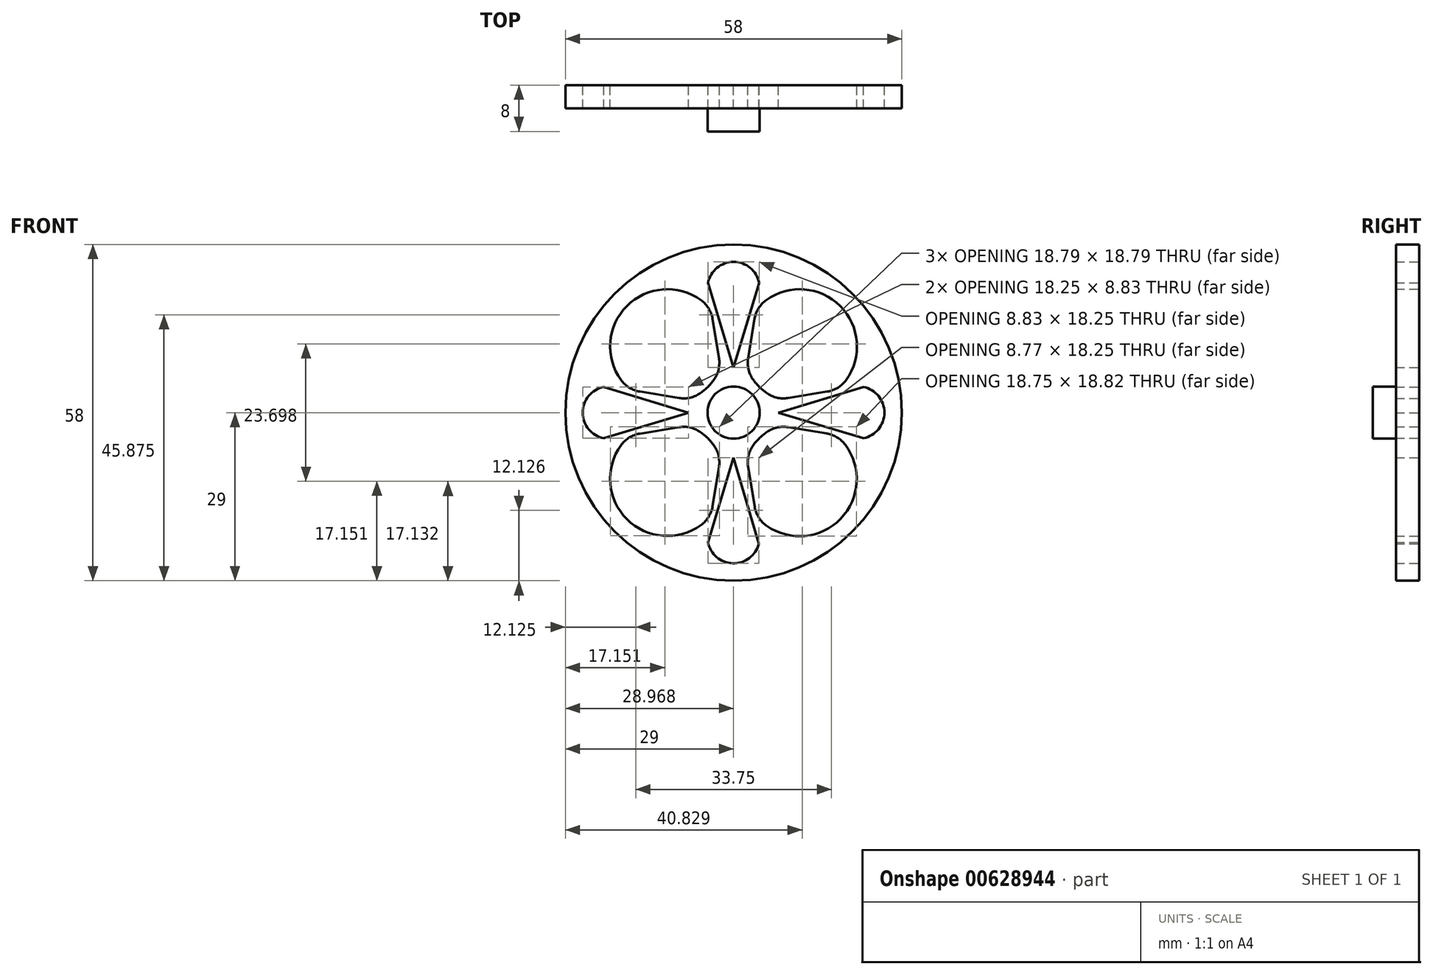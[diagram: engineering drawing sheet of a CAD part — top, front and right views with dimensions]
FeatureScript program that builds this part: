
annotation { "Feature Type Name" : "Feature", "Feature Type Description" : "" }
export const myFeature = defineFeature(function(context is Context, id is Id, definition is map)
    precondition{}
    {
        {
            var Q0;
            Q0=qCreatedBy(makeId("Front.planeOp"),FACE);
            var sketch = newSketch(context, id + "F0", { "sketchPlane" : qUnion([Q0])});
            skCircle(sketch, "E0", {"center": v(0, 0) * mm, "radius": 27 * mm});
            skCircle(sketch, "E1", {"center": v(0, 0) * mm, "radius": 4.5 * mm});
            skCircle(sketch, "E2", {"center": v(0, 0) * mm, "radius": 29 * mm});
            skArc(sketch, "E3", {"start": v(-22.37, 4.42) * mm, "mid": v(-26, 0) * mm, "end": v(-22.37, -4.42) * mm});
            skArc(sketch, "E4", {"start": v(4.42, 22.37) * mm, "mid": v(0, 26) * mm, "end": v(-4.42, 22.37) * mm});
            skArc(sketch, "E5", {"start": v(22.37, -4.42) * mm, "mid": v(26, 0) * mm, "end": v(22.37, 4.42) * mm});
            skArc(sketch, "E6", {"start": v(-4.42, -22.37) * mm, "mid": v(-0.14, -26) * mm, "end": v(4.35, -22.65) * mm});
            skPoint(sketch, "E7.orphan", {"position": v(-55.65, 0) * mm});
            skLineSegment(sketch, "E8", {"start": v(-16.16, 3.63) * mm, "end": v(-9.39, 2.52) * mm});
            skLineSegment(sketch, "E9", {"start": v(-16.16, -3.63) * mm, "end": v(-9.39, -2.52) * mm});
            skLineSegment(sketch, "E10", {"start": v(-2.52, -9.39) * mm, "end": v(-3.63, -16.16) * mm});
            skLineSegment(sketch, "E11", {"start": v(2.52, -9.37) * mm, "end": v(3.64, -16.26) * mm});
            skLineSegment(sketch, "E12", {"start": v(9.4, -2.52) * mm, "end": v(16.06, -3.6) * mm});
            skLineSegment(sketch, "E13", {"start": v(9.39, 2.52) * mm, "end": v(16.16, 3.63) * mm});
            skLineSegment(sketch, "E14", {"start": v(2.52, 9.39) * mm, "end": v(3.63, 16.16) * mm});
            skArc(sketch, "E15", {"start": v(5.76, -3.34) * mm, "mid": v(4.5, -4.37) * mm, "end": v(3.43, -5.6) * mm});
            skPoint(sketch, "E15.third.point", {"position": v(18.33, -18.44) * mm});
            skArc(sketch, "E16", {"start": v(19.4, 5.63) * mm, "mid": v(18.38, 18.38) * mm, "end": v(5.63, 19.4) * mm});
            skPoint(sketch, "E16.third.point", {"position": v(16.77, 19.7) * mm});
            skArc(sketch, "E17", {"start": v(-19.4, -5.63) * mm, "mid": v(-18.38, -18.38) * mm, "end": v(-5.63, -19.4) * mm});
            skPoint(sketch, "E17.third.point", {"position": v(-19.92, -16.4) * mm});
            skArc(sketch, "E18", {"start": v(-5.67, 3.38) * mm, "mid": v(-4.43, 4.43) * mm, "end": v(-3.38, 5.67) * mm});
            skPoint(sketch, "E18.third.point", {"position": v(-19.3, 17.32) * mm});
            skLineSegment(sketch, "E19", {"start": v(0, 7.75) * mm, "end": v(-4.42, 22.37) * mm});
            skLineSegment(sketch, "E20", {"start": v(4.42, 22.37) * mm, "end": v(0, 7.75) * mm});
            skLineSegment(sketch, "E21", {"start": v(7.75, 0) * mm, "end": v(14.26, 1.97) * mm});
            skLineSegment(sketch, "E22", {"start": v(22.37, -4.42) * mm, "end": v(7.75, 0) * mm});
            skLineSegment(sketch, "E23", {"start": v(-7.75, 0) * mm, "end": v(-22.37, 4.42) * mm});
            skLineSegment(sketch, "E24", {"start": v(-22.37, -4.42) * mm, "end": v(-7.75, 0) * mm});
            skLineSegment(sketch, "E25", {"start": v(0, -7.75) * mm, "end": v(-4.42, -22.37) * mm});
            skLineSegment(sketch, "E26", {"start": v(4.35, -22.65) * mm, "end": v(0, -7.75) * mm});
            skArc(sketch, "E27.trimOffspring", {"start": v(-3.38, -5.67) * mm, "mid": v(-4.43, -4.43) * mm, "end": v(-5.67, -3.38) * mm});
            skArc(sketch, "E28.trimOffspring", {"start": v(5.71, -19.55) * mm, "mid": v(18.45, -18.32) * mm, "end": v(19.26, -5.55) * mm});
            skLineSegment(sketch, "E29", {"start": v(14.26, 1.97) * mm, "end": v(22.37, 4.42) * mm});
            skArc(sketch, "E30.trimOffspring", {"start": v(3.38, 5.67) * mm, "mid": v(4.43, 4.43) * mm, "end": v(5.67, 3.38) * mm});
            skArc(sketch, "E31.trimOffspring", {"start": v(-5.63, 19.4) * mm, "mid": v(-18.38, 18.38) * mm, "end": v(-19.4, 5.63) * mm});
            skLineSegment(sketch, "E32.trimOffspring", {"start": v(-3.63, 16.16) * mm, "end": v(-2.52, 9.39) * mm});
            skPoint(sketch, "E33.visualSharp", {"position": v(-7.75, 2.25) * mm});
            skArc(sketch, "E33.filletArc", {"start": v(-9.39, 2.52) * mm, "mid": v(-7.45, 2.58) * mm, "end": v(-5.67, 3.38) * mm});
            skPoint(sketch, "E34.visualSharp", {"position": v(-17.8, 3.9) * mm});
            skArc(sketch, "E34.filletArc", {"start": v(-19.4, 5.63) * mm, "mid": v(-17.98, 4.3) * mm, "end": v(-16.16, 3.63) * mm});
            skPoint(sketch, "E35.visualSharp", {"position": v(-3.9, 17.8) * mm});
            skArc(sketch, "E35.filletArc", {"start": v(-3.63, 16.16) * mm, "mid": v(-4.3, 17.98) * mm, "end": v(-5.63, 19.4) * mm});
            skPoint(sketch, "E36.visualSharp", {"position": v(-2.25, 7.75) * mm});
            skArc(sketch, "E36.filletArc", {"start": v(-3.38, 5.67) * mm, "mid": v(-2.58, 7.45) * mm, "end": v(-2.52, 9.39) * mm});
            skPoint(sketch, "E37.visualSharp", {"position": v(7.8, -2.26) * mm});
            skArc(sketch, "E37.filletArc", {"start": v(9.4, -2.52) * mm, "mid": v(7.5, -2.58) * mm, "end": v(5.76, -3.34) * mm});
            skPoint(sketch, "E38.visualSharp", {"position": v(2.24, -7.7) * mm});
            skArc(sketch, "E38.filletArc", {"start": v(3.43, -5.6) * mm, "mid": v(2.6, -7.4) * mm, "end": v(2.52, -9.37) * mm});
            skPoint(sketch, "E39.visualSharp", {"position": v(17.66, -3.87) * mm});
            skArc(sketch, "E39.filletArc", {"start": v(19.26, -5.55) * mm, "mid": v(17.85, -4.27) * mm, "end": v(16.06, -3.6) * mm});
            skPoint(sketch, "E40.visualSharp", {"position": v(-2.25, -7.75) * mm});
            skArc(sketch, "E40.filletArc", {"start": v(-2.52, -9.39) * mm, "mid": v(-2.58, -7.45) * mm, "end": v(-3.38, -5.67) * mm});
            skPoint(sketch, "E41.visualSharp", {"position": v(-7.75, -2.25) * mm});
            skArc(sketch, "E41.filletArc", {"start": v(-5.67, -3.38) * mm, "mid": v(-7.45, -2.58) * mm, "end": v(-9.39, -2.52) * mm});
            skPoint(sketch, "E42.visualSharp", {"position": v(3.92, -17.93) * mm});
            skArc(sketch, "E42.filletArc", {"start": v(3.64, -16.26) * mm, "mid": v(4.34, -18.11) * mm, "end": v(5.71, -19.55) * mm});
            skPoint(sketch, "E43.visualSharp", {"position": v(-3.9, -17.8) * mm});
            skArc(sketch, "E43.filletArc", {"start": v(-5.63, -19.4) * mm, "mid": v(-4.3, -17.98) * mm, "end": v(-3.63, -16.16) * mm});
            skPoint(sketch, "E44.visualSharp", {"position": v(-17.8, -3.9) * mm});
            skArc(sketch, "E44.filletArc", {"start": v(-16.16, -3.63) * mm, "mid": v(-17.98, -4.3) * mm, "end": v(-19.4, -5.63) * mm});
            skPoint(sketch, "E45.visualSharp", {"position": v(17.8, 3.9) * mm});
            skArc(sketch, "E45.filletArc", {"start": v(16.16, 3.63) * mm, "mid": v(17.98, 4.3) * mm, "end": v(19.4, 5.63) * mm});
            skPoint(sketch, "E46.visualSharp", {"position": v(7.75, 2.25) * mm});
            skArc(sketch, "E46.filletArc", {"start": v(5.67, 3.38) * mm, "mid": v(7.45, 2.58) * mm, "end": v(9.39, 2.52) * mm});
            skPoint(sketch, "E47.visualSharp", {"position": v(2.25, 7.75) * mm});
            skArc(sketch, "E47.filletArc", {"start": v(2.52, 9.39) * mm, "mid": v(2.58, 7.45) * mm, "end": v(3.38, 5.67) * mm});
            skPoint(sketch, "E48.visualSharp", {"position": v(3.9, 17.8) * mm});
            skArc(sketch, "E48.filletArc", {"start": v(5.63, 19.4) * mm, "mid": v(4.3, 17.98) * mm, "end": v(3.63, 16.16) * mm});
            skSolve(sketch);
        }
        {
            var Q0;
            Q0=makeQuery(id+"F0.imprint","IMPRINT",FACE,{"disambiguationData":[TD([[makeQuery(id+"F0.imprint","IMPRINT",EDGE,{"derivedFrom":sQuery(id+"F0.wireOp",EDGE,"E1")}),1.0]])]});
            extrude(context, id + "F1", {"entities" : qUnion([Q0]), "depth" : 8 * mm, "offsetDistance" : 25 * mm});
        }
        {
            var Q0;
            Q0=makeQuery(id+"F0.imprint","IMPRINT",FACE,{"disambiguationData":[TD([[makeQuery(id+"F0.imprint","IMPRINT",EDGE,{"derivedFrom":sQuery(id+"F0.wireOp",EDGE,"E0")}),1.0]])]});
            var Q1;
            Q1=makeQuery(id+"F0.imprint","IMPRINT",FACE,{"disambiguationData":[TD([[makeQuery(id+"F0.imprint","IMPRINT",EDGE,{"derivedFrom":sQuery(id+"F0.wireOp",EDGE,"E0")}),-1.0]])]});
            extrude(context, id + "F2", {"entities" : qUnion([Q0, Q1]), "operationType" : NewBodyOperationType.ADD, "depth" : 4 * mm, "offsetDistance" : 25 * mm});
        }
    });
